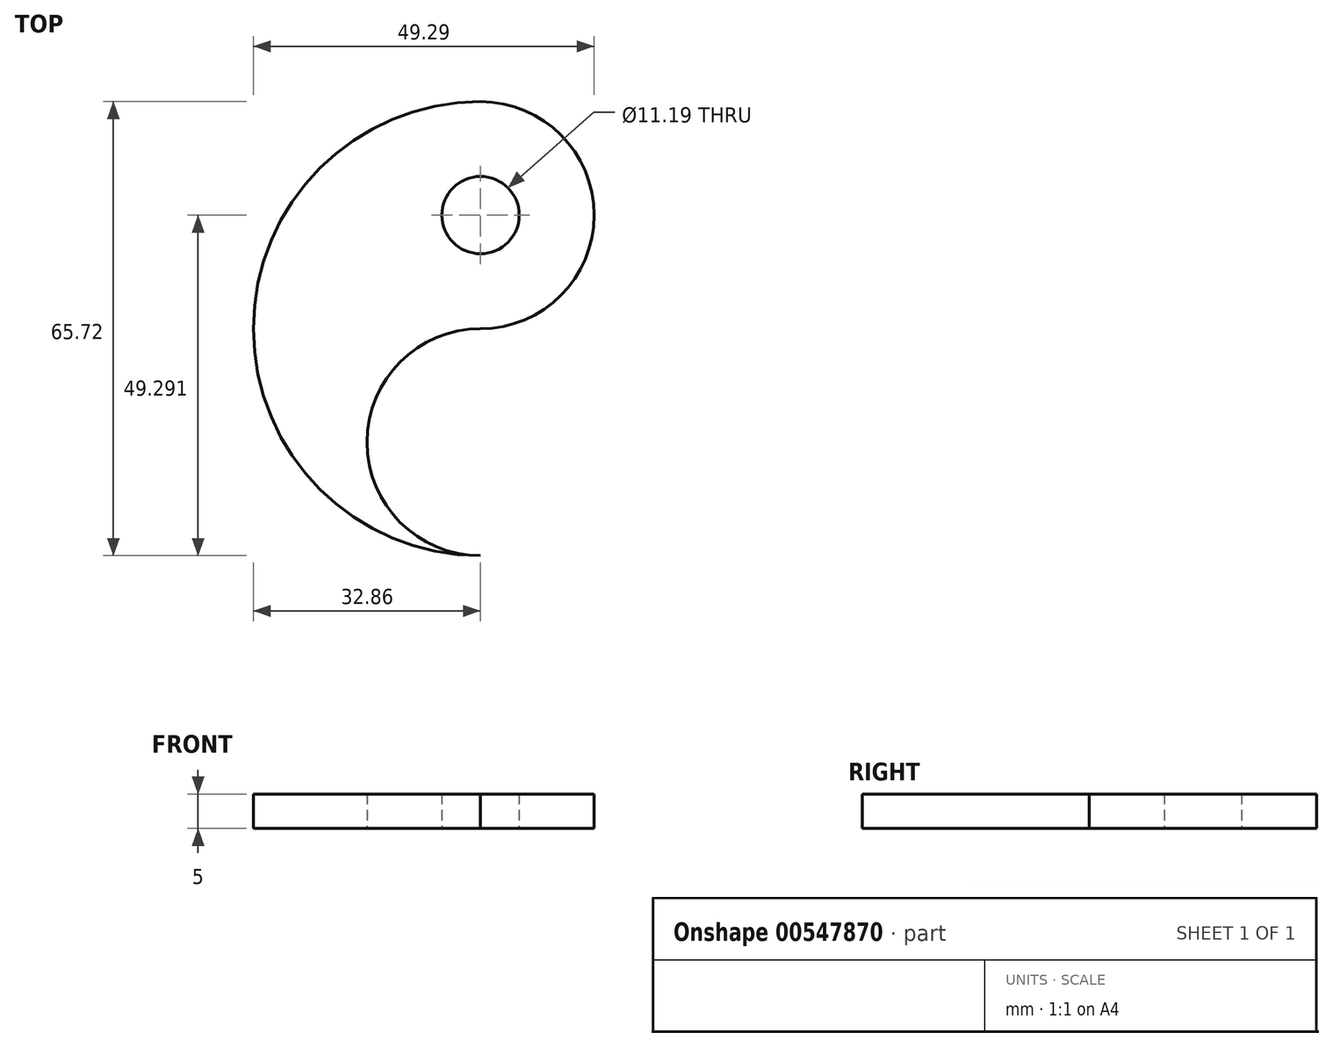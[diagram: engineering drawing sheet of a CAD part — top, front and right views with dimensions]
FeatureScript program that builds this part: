
annotation { "Feature Type Name" : "Feature", "Feature Type Description" : "" }
export const myFeature = defineFeature(function(context is Context, id is Id, definition is map)
    precondition{}
    {
        {
            var Q0;
            Q0=qCreatedBy(makeId("Top.planeOp"),FACE);
            var sketch = newSketch(context, id + "F0", { "sketchPlane" : qUnion([Q0])});
            skArc(sketch, "E0", {"start": v(0, 32.86) * mm, "mid": v(-32.86, 0) * mm, "end": v(0, -32.86) * mm});
            skLineSegment(sketch, "E1", {"start": v(0, 0) * mm, "end": v(0, 0) * mm});
            skArc(sketch, "E2", {"start": v(0, 0) * mm, "mid": v(-16.43, -16.43) * mm, "end": v(0, -32.86) * mm});
            skArc(sketch, "E3", {"start": v(0, 0) * mm, "mid": v(16.43, 16.43) * mm, "end": v(0, 32.86) * mm});
            skCircle(sketch, "E4", {"center": v(0, 16.43) * mm, "radius": 5.6 * mm});
            skSolve(sketch);
        }
        {
            var Q0;
            Q0=makeQuery(id+"F0.imprint","IMPRINT",FACE,{"disambiguationData":[TD([[makeQuery(id+"F0.imprint","IMPRINT",EDGE,{"derivedFrom":sQuery(id+"F0.wireOp",EDGE,"E0")}),1.0]])]});
            extrude(context, id + "F1", {"entities" : qUnion([Q0]), "depth" : 5 * mm, "offsetDistance" : 25 * mm});
        }
    });
